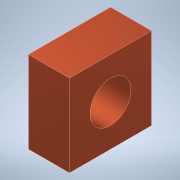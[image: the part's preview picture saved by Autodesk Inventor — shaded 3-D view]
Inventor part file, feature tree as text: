
AUTODESK INVENTOR PART (.ipt)
format: ipt  version: 2022 (Build 260153000, 153)  size: 97,792 bytes
history: native  units: mm
features: extrude x1, sketch x1
ambient origin geometry x8: Origin, YZ Plane, XZ Plane, XY Plane, X Axis, Y Axis, Z Axis, Center Point
bodies: Solid1 (feature_tree)
feature tree (2):
  extrude  "Extrusion1"  Depth=10.0mm
  sketch  "Sketch1"  dims[d0=10.0mm d1=10.0mm d2=5.0mm d3=5.0mm d4=0.0mm]
